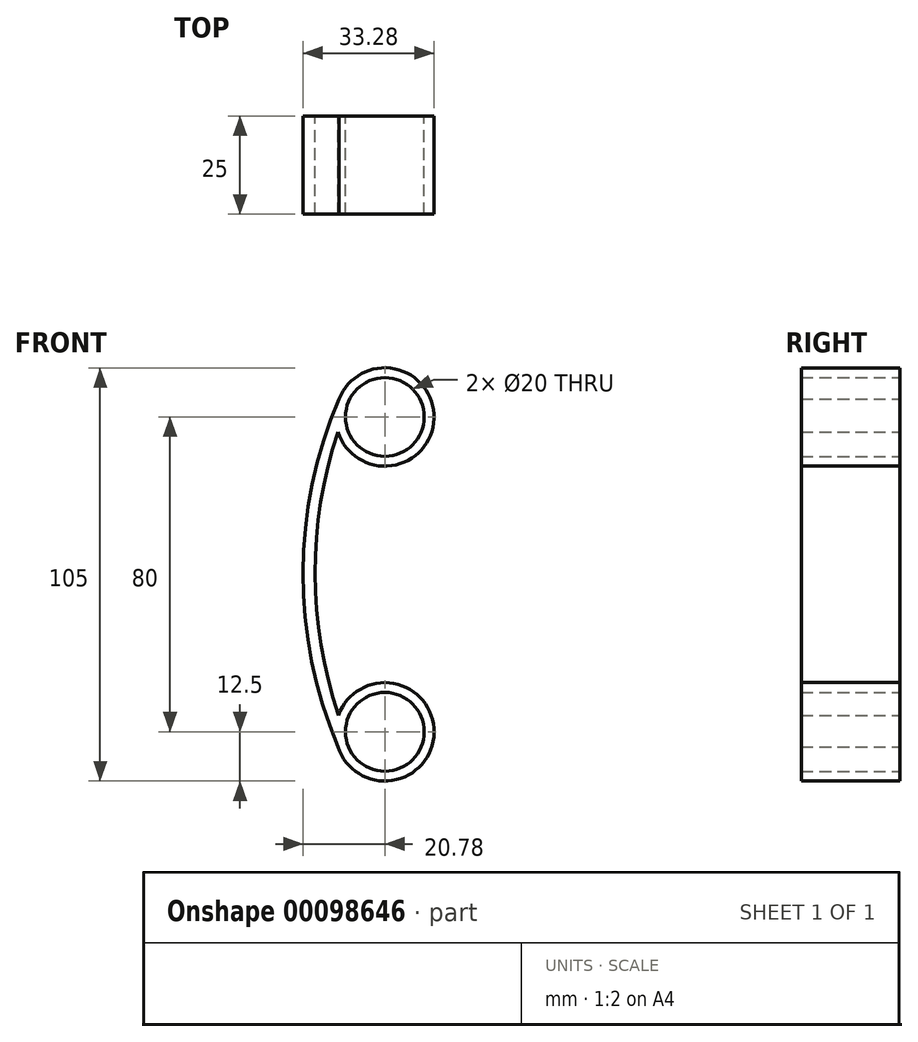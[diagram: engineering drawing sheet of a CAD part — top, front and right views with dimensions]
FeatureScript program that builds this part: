
annotation { "Feature Type Name" : "Feature", "Feature Type Description" : "" }
export const myFeature = defineFeature(function(context is Context, id is Id, definition is map)
    precondition{}
    {
        {
            var Q0;
            Q0=qCreatedBy(makeId("Front.planeOp"),FACE);
            var sketch = newSketch(context, id + "F0", { "sketchPlane" : qUnion([Q0])});
            skLineSegment(sketch, "E0", {"start": v(0, 40) * mm, "end": v(0, -40) * mm, "construction": true});
            skCircle(sketch, "E1", {"center": v(0, 40) * mm, "radius": 10 * mm});
            skCircle(sketch, "E2", {"center": v(0, 40) * mm, "radius": 12.5 * mm});
            skCircle(sketch, "E3", {"center": v(0, -40) * mm, "radius": 10 * mm});
            skCircle(sketch, "E4", {"center": v(0, -40) * mm, "radius": 12.5 * mm});
            skArc(sketch, "E5", {"start": v(-11.64, 44.57) * mm, "mid": v(-20.78, 0.4) * mm, "end": v(-11.9, -43.84) * mm});
            skArc(sketch, "E6", {"start": v(-9.8, 42) * mm, "mid": v(-17.72, 0.67) * mm, "end": v(-9.98, -40.68) * mm});
            skArc(sketch, "E7.MirrorCS", {"start": v(9.8, 42) * mm, "mid": v(17.72, 0.67) * mm, "end": v(9.98, -40.68) * mm});
            skArc(sketch, "E8.MirrorCS", {"start": v(11.64, 44.57) * mm, "mid": v(20.78, 0.4) * mm, "end": v(11.9, -43.84) * mm});
            skSolve(sketch);
        }
        {
            var Q0;
            Q0=makeQuery(id+"F0.imprint","IMPRINT",FACE,{"disambiguationData":[TD([[makeQuery(id+"F0.imprint","IMPRINT",EDGE,{"derivedFrom":sQuery(id+"F0.wireOp",EDGE,"E1")}),-1.0]])]});
            var Q1;
            {var subQ0=sQuery(id+"F0.wireOp",EDGE,"E5");Q1=makeQuery(id+"F0.imprint","IMPRINT",FACE,{"disambiguationData":[TD([[makeQuery(id+"F0.imprint","IMPRINT",EDGE,{"derivedFrom":subQ0}),1.0]])]});}
            var Q2;
            Q2=makeQuery(id+"F0.imprint","IMPRINT",FACE,{"disambiguationData":[TD([[makeQuery(id+"F0.imprint","IMPRINT",EDGE,{"derivedFrom":sQuery(id+"F0.wireOp",EDGE,"E3")}),-1.0]])]});
            var Q3;
            {var subQ4=sQuery(id+"F0.wireOp",EDGE,"E1");var subQ7=sQuery(id+"F0.wireOp",EDGE,"E6");var subQ9=makeQuery(id+"F0.imprint","INTERSECT",VERTEX,{"derivedFrom":[subQ4,subQ7]});Q3=makeQuery(id+"F0.imprint","IMPRINT",FACE,{"disambiguationData":[TD([[makeQuery(id+"F0.imprint","IMPRINT",EDGE,{"disambiguationData":[TD([[subQ9,1.0]])],"derivedFrom":subQ4}),-1.0]])]});}
            var Q4;
            {var subQ0=sQuery(id+"F0.wireOp",EDGE,"E8.MirrorCS");Q4=makeQuery(id+"F0.imprint","IMPRINT",FACE,{"disambiguationData":[TD([[makeQuery(id+"F0.imprint","IMPRINT",EDGE,{"derivedFrom":subQ0}),-1.0]])]});}
            var Q5;
            {var subQ5=sQuery(id+"F0.wireOp",EDGE,"E6");var subQ7=sQuery(id+"F0.wireOp",EDGE,"E3");var subQ8=makeQuery(id+"F0.imprint","INTERSECT",VERTEX,{"derivedFrom":[subQ7,subQ5]});Q5=makeQuery(id+"F0.imprint","IMPRINT",FACE,{"disambiguationData":[TD([[makeQuery(id+"F0.imprint","IMPRINT",EDGE,{"disambiguationData":[TD([[subQ8,-1.0]])],"derivedFrom":subQ7}),-1.0]])]});}
            extrude(context, id + "F1", {"entities" : qUnion([Q0, Q1, Q2, Q3, Q4, Q5]), "depth" : 25 * mm});
        }
    });
